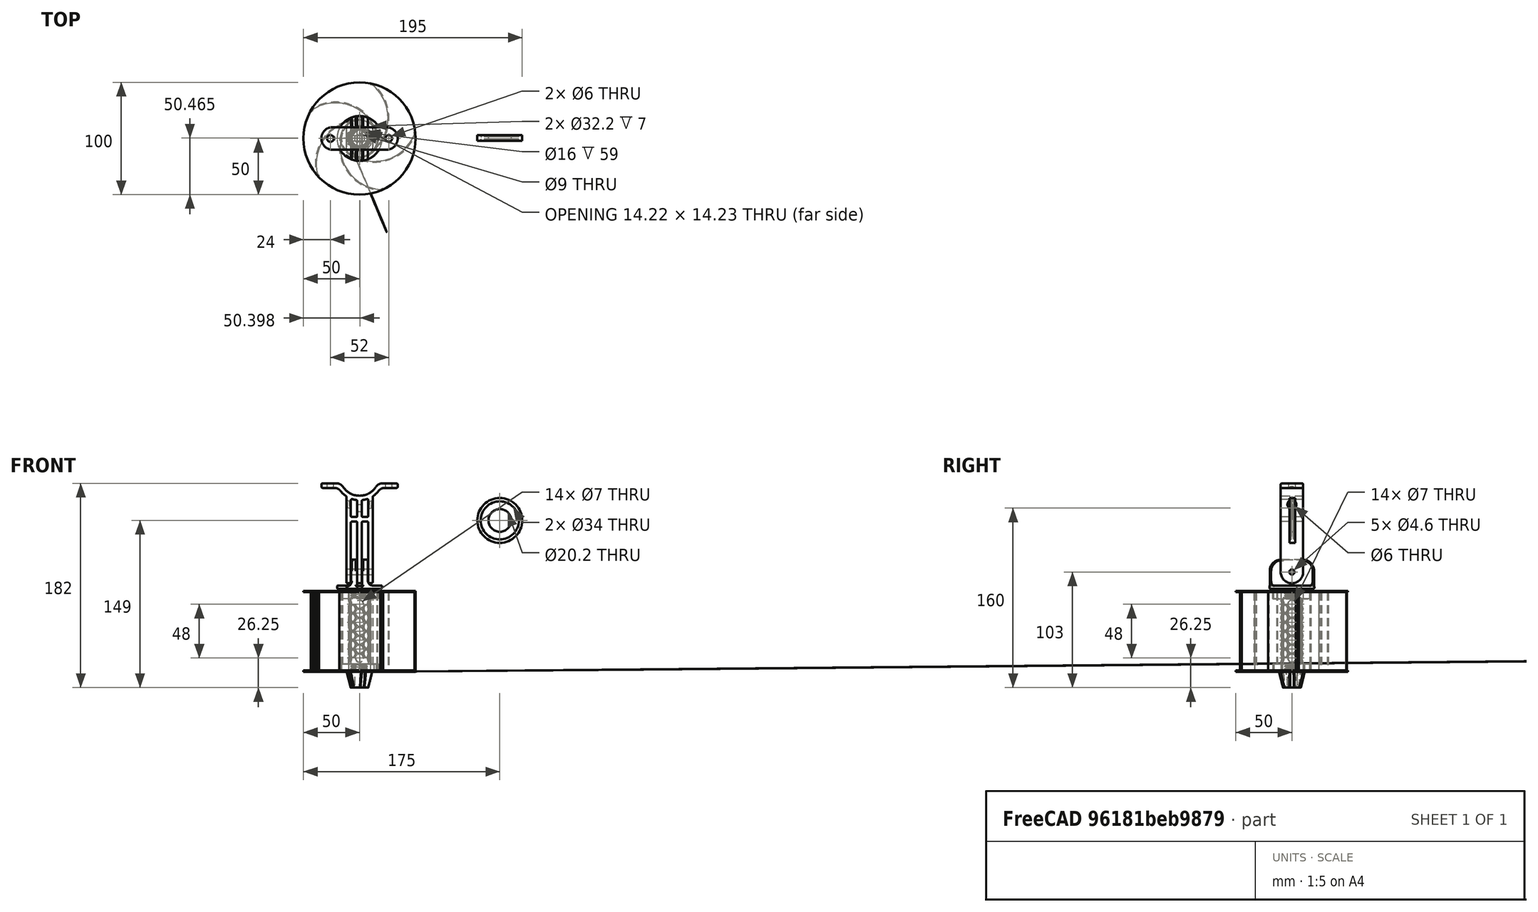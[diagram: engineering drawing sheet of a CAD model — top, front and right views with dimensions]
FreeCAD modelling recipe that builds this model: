
FCSTD DOCUMENT  (FreeCAD 1.1R40077 (Git))
Label: NES-sampler
License: All rights reserved
LicenseURL: http://en.wikipedia.org/wiki/All_rights_reserved
objects: Part::Cylinder×77, Part::MultiFuse×25, Part::Cut×25, Part::Box×21, Part::Fillet×11, Part::Part2DObjectPython×6, Part::Cone×6, Part::MultiCommon×5, Part::Helix×4, Part::Sweep×4
note: 184 computed .brp shape members not serialized (recipe doc carries the construction recipe); baked Part::Feature solids carry a one-line shape summary decoded from their .brp

FEATURE [Part::Cylinder] Cylinder079
  Angle = 360
  AttacherType = Attacher::AttachEngine3D
  FirstAngle = 0
  Height = 26
  Placement = pos=(0,13,62) rot=(1,0,0;1.5708rad)
  Radius = 3.5
  SecondAngle = 0
FEATURE [Part::Cylinder] Cylinder082
  Angle = 360
  AttacherType = Attacher::AttachEngine3D
  FirstAngle = 0
  Height = 26
  Placement = pos=(0,13,22) rot=(1,0,0;1.5708rad)
  Radius = 3.5
  SecondAngle = 0
FEATURE [Part::Cylinder] Cylinder083
  Angle = 360
  AttacherType = Attacher::AttachEngine3D
  FirstAngle = 0
  Height = 26
  Placement = pos=(0,13,54) rot=(1,0,0;1.5708rad)
  Radius = 3.5
  SecondAngle = 0
FEATURE [Part::Cylinder] Cylinder084
  Angle = 360
  AttacherType = Attacher::AttachEngine3D
  FirstAngle = 0
  Height = 26
  Placement = pos=(0,13,46) rot=(1,0,0;1.5708rad)
  Radius = 3.5
  SecondAngle = 0
FEATURE [Part::Cylinder] Cylinder085
  Angle = 360
  AttacherType = Attacher::AttachEngine3D
  FirstAngle = 0
  Height = 26
  Placement = pos=(0,13,30) rot=(1,0,0;1.5708rad)
  Radius = 3.5
  SecondAngle = 0
FEATURE [Part::Cylinder] Cylinder086
  Angle = 360
  AttacherType = Attacher::AttachEngine3D
  FirstAngle = 0
  Height = 26
  Placement = pos=(0,13,62) rot=(1,0,0;1.5708rad)
  Radius = 3.5
  SecondAngle = 0
FEATURE [Part::Cylinder] Cylinder087
  Angle = 360
  AttacherType = Attacher::AttachEngine3D
  FirstAngle = 0
  Height = 26
  Placement = pos=(0,13,14) rot=(1,0,0;1.5708rad)
  Radius = 3.5
  SecondAngle = 0
FEATURE [Part::Cylinder] Cylinder088
  Angle = 360
  AttacherType = Attacher::AttachEngine3D
  FirstAngle = 0
  Height = 26
  Placement = pos=(0,13,38) rot=(1,0,0;1.5708rad)
  Radius = 3.5
  SecondAngle = 0
FEATURE [Part::Cylinder] Cylinder104
  Angle = 360
  AttacherType = Attacher::AttachEngine3D
  FirstAngle = 0
  Height = 77
  Placement = pos=(0,0,3) rot=(0,0,1;0rad)
  Radius = 8
  SecondAngle = 0
FEATURE [Part::Cylinder] Cylinder106
  Angle = 360
  AttacherType = Attacher::AttachEngine3D
  FirstAngle = 0
  Height = 73
  Placement = pos=(0,0,4.26) rot=(0,0,1;0rad)
  Radius = 9.8
  SecondAngle = 0
FEATURE [Part::Cylinder] Cylinder166
  Angle = 360
  AttacherType = Attacher::AttachEngine3D
  FirstAngle = 0
  Height = 26
  Placement = pos=(0,13,53) rot=(1,0,0;1.5708rad)
  Radius = 3.5
  SecondAngle = 0
FEATURE [Part::Cylinder] Cylinder167
  Angle = 360
  AttacherType = Attacher::AttachEngine3D
  FirstAngle = 0
  Height = 26
  Placement = pos=(0,13,21) rot=(1,0,0;1.5708rad)
  Radius = 3.5
  SecondAngle = 0
FEATURE [Part::Cylinder] Cylinder168
  Angle = 360
  AttacherType = Attacher::AttachEngine3D
  FirstAngle = 0
  Height = 26
  Placement = pos=(0,13,29) rot=(1,0,0;1.5708rad)
  Radius = 3.5
  SecondAngle = 0
FEATURE [Part::Cylinder] Cylinder169
  Angle = 360
  AttacherType = Attacher::AttachEngine3D
  FirstAngle = 0
  Height = 26
  Placement = pos=(0,13,37) rot=(1,0,0;1.5708rad)
  Radius = 3.5
  SecondAngle = 0
FEATURE [Part::Cylinder] Cylinder170
  Angle = 360
  AttacherType = Attacher::AttachEngine3D
  FirstAngle = 0
  Height = 26
  Placement = pos=(0,13,61) rot=(1,0,0;1.5708rad)
  Radius = 3.5
  SecondAngle = 0
FEATURE [Part::Cylinder] Cylinder171
  Angle = 360
  AttacherType = Attacher::AttachEngine3D
  FirstAngle = 0
  Height = 26
  Placement = pos=(0,13,45) rot=(1,0,0;1.5708rad)
  Radius = 3.5
  SecondAngle = 0
FEATURE [Part::Cylinder] Cylinder172
  Angle = 360
  AttacherType = Attacher::AttachEngine3D
  FirstAngle = 0
  Height = 26
  Placement = pos=(0,13,22) rot=(1,0,0;1.5708rad)
  Radius = 3.5
  SecondAngle = 0
FEATURE [Part::Cylinder] Cylinder173
  Angle = 360
  AttacherType = Attacher::AttachEngine3D
  FirstAngle = 0
  Height = 26
  Placement = pos=(0,13,30) rot=(1,0,0;1.5708rad)
  Radius = 3.5
  SecondAngle = 0
FEATURE [Part::Cylinder] Cylinder174
  Angle = 360
  AttacherType = Attacher::AttachEngine3D
  FirstAngle = 0
  Height = 26
  Placement = pos=(0,13,38) rot=(1,0,0;1.5708rad)
  Radius = 3.5
  SecondAngle = 0
FEATURE [Part::Cylinder] Cylinder175
  Angle = 360
  AttacherType = Attacher::AttachEngine3D
  FirstAngle = 0
  Height = 26
  Placement = pos=(0,13,46) rot=(1,0,0;1.5708rad)
  Radius = 3.5
  SecondAngle = 0
FEATURE [Part::Cylinder] Cylinder176
  Angle = 360
  AttacherType = Attacher::AttachEngine3D
  FirstAngle = 0
  Height = 26
  Placement = pos=(0,13,54) rot=(1,0,0;1.5708rad)
  Radius = 3.5
  SecondAngle = 0
FEATURE [Part::Cylinder] Cylinder177
  Angle = 360
  AttacherType = Attacher::AttachEngine3D
  FirstAngle = 0
  Height = 26
  Placement = pos=(0,13,14) rot=(1,0,0;1.5708rad)
  Radius = 3.5
  SecondAngle = 0
FEATURE [Part::Cylinder] Cylinder178
  Angle = 360
  AttacherType = Attacher::AttachEngine3D
  FirstAngle = 0
  Height = 26
  Placement = pos=(0,13,62) rot=(1,0,0;1.5708rad)
  Radius = 3.5
  SecondAngle = 0
FEATURE [Part::Cylinder] Cylinder179
  Angle = 360
  AttacherType = Attacher::AttachEngine3D
  FirstAngle = 0
  Height = 26
  Placement = pos=(0,13,29) rot=(1,0,0;1.5708rad)
  Radius = 3.5
  SecondAngle = 0
FEATURE [Part::Cylinder] Cylinder180
  Angle = 360
  AttacherType = Attacher::AttachEngine3D
  FirstAngle = 0
  Height = 26
  Placement = pos=(0,13,45) rot=(1,0,0;1.5708rad)
  Radius = 3.5
  SecondAngle = 0
FEATURE [Part::Cylinder] Cylinder181
  Angle = 360
  AttacherType = Attacher::AttachEngine3D
  FirstAngle = 0
  Height = 26
  Placement = pos=(0,13,61) rot=(1,0,0;1.5708rad)
  Radius = 3.5
  SecondAngle = 0
FEATURE [Part::Cylinder] Cylinder182
  Angle = 360
  AttacherType = Attacher::AttachEngine3D
  FirstAngle = 0
  Height = 26
  Placement = pos=(0,13,37) rot=(1,0,0;1.5708rad)
  Radius = 3.5
  SecondAngle = 0
FEATURE [Part::Cylinder] Cylinder183
  Angle = 360
  AttacherType = Attacher::AttachEngine3D
  FirstAngle = 0
  Height = 26
  Placement = pos=(0,13,21) rot=(1,0,0;1.5708rad)
  Radius = 3.5
  SecondAngle = 0
FEATURE [Part::Cylinder] Cylinder184
  Angle = 360
  AttacherType = Attacher::AttachEngine3D
  FirstAngle = 0
  Height = 26
  Placement = pos=(0,13,53) rot=(1,0,0;1.5708rad)
  Radius = 3.5
  SecondAngle = 0
FEATURE [Part::MultiFuse] Fusion113
  Placement = pos=(0,0,2) rot=(0,0,1;0rad)
  Shapes = -> [Cylinder088,Cylinder079,Cylinder083,Cylinder082,Cylinder085,Cylinder087,Cylinder086,Cylinder084]
FEATURE [Part::MultiFuse] Fusion114
  Placement = pos=(0,0,-1) rot=(0,0,1;0.785398rad)
  Shapes = -> [Cylinder169,Cylinder168,Cylinder171,Cylinder170,Cylinder167,Cylinder166]
FEATURE [Part::MultiFuse] Fusion115
  Placement = pos=(0,0,-1) rot=(0,0,-1;0.785398rad)
  Shapes = -> [Cylinder182,Cylinder179,Cylinder180,Cylinder181,Cylinder183,Cylinder184]
FEATURE [Part::MultiFuse] Fusion116
  Placement = pos=(0,0,2) rot=(0,0,1;1.5708rad)
  Shapes = -> [Cylinder177,Cylinder172,Cylinder173,Cylinder174,Cylinder175,Cylinder176,Cylinder178]
FEATURE [Part::MultiFuse] Fusion190
  Placement = pos=(0,0,0.5) rot=(0,0,1;0rad)
  Shapes = -> [Fusion116,Fusion115,Fusion114,Fusion113]
FEATURE [Part::MultiFuse] Fusion191
  Shapes = -> [Cylinder104,Fusion190]
FEATURE [Part::Cut] Cut036
  Base = -> Cylinder106
  Placement = pos=(0,0,35.75) rot=(0,0,1;0rad)
  Tool = -> Fusion191
FEATURE [Part::Helix] Helix001
  Angle = 0
  AttacherType = Attacher::AttachEngine3D
  Height = 10
  Length = 231.123
  LocalCoord = 0
  Pitch = 2
  Radius = 7.35
  SegmentLength = 1
  Style = 0
  expr: AttachmentOffset = VThreadProfile001.AttachmentOffset
  expr: Height = VThreadProfile001.ThreadCount * VThreadProfile001.Pitch
  expr: MapMode = VThreadProfile001.MapMode
  expr: MapPathParameter = VThreadProfile001.MapPathParameter
  expr: MapReversed = VThreadProfile001.MapReversed
  expr: Pitch = VThreadProfile001.Pitch
  expr: SegmentLength = 1
FEATURE [Part::Part2DObjectPython] VThreadProfile001  # Draft 2D object (typed FeaturePython)
  Area = 186.808
  Closed = true
  Continuity = C2
  Height = 10
  Helix = Helix
  Instructions = Expand this with the ... button to view instructions | Sweep this object along a helix of the same pitch to produce your thread. | It is recommended to make the helix in the ThreadProfile workbench. | If there is an active Body the ThreadProfile object will be put into it.,If not it can be dragged and dropped into the body later. | If there is an active Body when the helix is made there will be made a ShapeBinder for it | For internal threads you will need to cut the Sweep object out of a cylinder, or if using Part Design sweep it as a Subtractive Pipe. | Always use Frenet mode | I have provided some presets, but it is possible there could be some errors.  Double check for mission critical applications. | Also, the tolerances might be different from what you wish to have.  I believe the internal minor diameters are all minimum and the external are all maximum.
  InternalOrExternal = 1
  MakeFace = true
  MinorDiameter = 14.5
  Parameterization = 1
  Pitch = 2
  Points = (66) [(7.21184,0.695393,0),(7.07086,1.3764,0),(6.87744,2.04019,0),(6.62901,2.68241,0),(6.32585,3.2984,0),(5.96952,3.88346,0),(5.56241,4.43304,0),+59 more]
  Presets = 0
  Quality = 11
  ThreadCount = 5
  Variants = 0
  Version = 1.89
  external2S_data = [-0.00461051,-0.00886426,-0.0128148,-0.0165028,-0.0199596,-0.0232105,-0.0262759,-0.0291725,-0.0319145,-0.0345137,-0.0369805,-0.0393235,-0.0415505,-0.0436681,-0.0456823,-0.0475981,-0.0494204,-0.0511532,-0.0528003,-0.0543649,-0.0558502,+698 more]
  external3S_data = [-0.00677828,-0.0128149,-0.0182584,-0.0232106,-0.0277444,-0.0319145,-0.0357632,-0.0393236,-0.0426227,-0.0456823,-0.0485208,-0.0511533,-0.0535928,-0.0558503,-0.0579353,-0.059856,-0.0616195,-0.0632319,-0.0646984,-0.0660239,-0.0672123,+698 more]
  external45_data = [-0.00137363,-0.00271738,-0.00403219,-0.00531893,-0.00657844,-0.00781148,-0.00901878,-0.010201,-0.0113589,-0.012493,-0.0136039,-0.0146921,-0.0157583,-0.0168028,-0.0178261,-0.0188288,-0.0198112,-0.0207738,-0.0217169,-0.0226409,-0.0235462,+698 more]
  external_data = [-0.00235387,-0.00461052,-0.00677828,-0.00886428,-0.0108747,-0.0128149,-0.0146895,-0.0165028,-0.0182584,-0.0199597,-0.0216095,-0.0232106,-0.0247653,-0.0262759,-0.0277444,-0.0291725,-0.0305621,-0.0319145,-0.0332313,-0.0345138,-0.0357632,+698 more]
  internal2S_data = [0,0,0,0,0,0,0,0,0,0,0,0,0,0,0,0,0,0,0,0,0,0,0,0,0,0,0,0,0,0,0,0,0,0,0,0,0,0,0,0,0,0,0,0,0,0,0,0,0,0,0,0,0,0,0,0,0,0,0,0,0,0,0,0,0,0,0,0,0,0,0,0,0,0,0,0,0,0,0,0,0,0,0,0,0,0,0,0,0,0,0.00481128,0.00962256,0.0144338,0.0192451,0.0240564,+624 more]
  internal3S_data = [0,0,0,0,0,0,0,0,0,0,0,0,0,0,0,0,0,0,0,0,0,0,0,0,0,0,0,0,0,0,0,0,0,0,0,0,0,0,0,0,0,0,0,0,0,0,0,0,0,0,0,0,0,0,0,0,0,0,0,0,0.00721688,0.0144338,0.0216506,0.0288675,0.0360844,0.0433013,0.0505181,0.057735,0.0649519,0.0721688,0.0793857,0.0866025,+647 more]
  internal45_data = [0,0,0,0,0,0,0,0,0,0,0,0,0,0,0,0,0,0,0,0,0,0,0,0,0,0,0,0,0,0,0,0,0,0,0,0,0,0,0,0,0,0,0,0,0,0,0,0,0,0,0,0,0,0,0,0,0,0,0,0,0,0,0,0,0,0,0,0,0,0,0,0,0,0,0,0,0,0,0,0,0,0,0,0,0,0,0,0,0,0,0,0,0,0,0,0,0,0,0,0,0,0,0,0,0,0,0,0,0,0,0,0,0,0,0,0,0,0,0,0,+599 more]
  internal_data = [0,0,0,0,0,0,0,0,0,0,0,0,0,0,0,0,0,0,0,0,0,0,0,0,0,0,0,0,0,0,0,0,0,0,0,0,0,0,0,0,0,0,0,0,0,0,0,0,0,0,0,0,0,0,0,0,0,0,0,0,0,0,0,0,0,0,0,0,0,0,0,0,0,0,0,0,0,0,0,0,0,0,0,0,0,0,0,0,0,0,0,0,0,0,0,0,0,0,0,0,0,0,0,0,0,0,0,0,0,0,0,0,0,0,0,0,0,0,0,0,+599 more]
  preset_names = <blob: 3959 chars omitted>
  presets_data = [0,0,0,2.20878,24.1173,24.6888,0.25,0.693,0.729,0.25,0.793,0.829,0.25,0.893,0.929,0.3,1.032,1.075,0.35,1.171,1.221,0.35,1.371,1.421,0.4,1.509,1.567,0.45,1.648,1.713,0.45,1.948,2.013,0.5,2.387,2.459,0.6,2.764,2.85,0.7,3.141,3.242,0.75,3.58,+712 more]
FEATURE [Part::Sweep] Sweep001  label="m16 wide"
  Frenet = true
  Placement = pos=(0,0,37) rot=(0,0,1;0rad)
  Sections = -> [VThreadProfile001]
  Solid = true
  Spine = -> Helix001 [Edge1,Edge2,Edge3,Edge4,Edge5]
  Transition = 1
FEATURE [Part::Cylinder] Cylinder
  Angle = 360
  AttacherType = Attacher::AttachEngine3D
  FirstAngle = 0
  Height = 7
  Placement = pos=(0,0,40) rot=(0,0,1;0rad)
  Radius = 9
  SecondAngle = 0
FEATURE [Part::Helix] Helix002
  Angle = 0
  AttacherType = Attacher::AttachEngine3D
  Height = 10
  Length = 231.123
  LocalCoord = 0
  Pitch = 2
  Radius = 7.35
  SegmentLength = 1
  Style = 0
  expr: AttachmentOffset = VThreadProfile002.AttachmentOffset
  expr: Height = VThreadProfile002.ThreadCount * VThreadProfile002.Pitch
  expr: MapMode = VThreadProfile002.MapMode
  expr: MapPathParameter = VThreadProfile002.MapPathParameter
  expr: MapReversed = VThreadProfile002.MapReversed
  expr: Pitch = VThreadProfile002.Pitch
  expr: SegmentLength = 1
FEATURE [Part::Part2DObjectPython] VThreadProfile002  # Draft 2D object (typed FeaturePython)
  Area = 186.808
  Closed = true
  Continuity = C2
  Height = 10
  Helix = Helix
  Instructions = <same value as first occurrence — deduplicated (x6 in doc)>
  InternalOrExternal = 1
  MakeFace = true
  MinorDiameter = 14.5
  Parameterization = 1
  Pitch = 2
  Points = (66) [(7.21184,0.695393,0),(7.07086,1.3764,0),(6.87744,2.04019,0),(6.62901,2.68241,0),(6.32585,3.2984,0),(5.96952,3.88346,0),(5.56241,4.43304,0),+59 more]
  Presets = 0
  Quality = 11
  ThreadCount = 5
  Variants = 0
  Version = 1.89
  external2S_data = <same value as first occurrence — deduplicated (x6 in doc)>
  external3S_data = <same value as first occurrence — deduplicated (x6 in doc)>
  external45_data = <same value as first occurrence — deduplicated (x6 in doc)>
  external_data = <same value as first occurrence — deduplicated (x6 in doc)>
  internal2S_data = <same value as first occurrence — deduplicated (x6 in doc)>
  internal3S_data = <same value as first occurrence — deduplicated (x6 in doc)>
  internal45_data = <same value as first occurrence — deduplicated (x6 in doc)>
  internal_data = <same value as first occurrence — deduplicated (x6 in doc)>
  preset_names = <blob: 3959 chars omitted>
  presets_data = <same value as first occurrence — deduplicated (x6 in doc)>
FEATURE [Part::Sweep] Sweep002  label="m16 wide001"
  Frenet = true
  Placement = pos=(0,0,106) rot=(0,0,1;0rad)
  Sections = -> [VThreadProfile002]
  Solid = true
  Spine = -> Helix002 [Edge1,Edge2,Edge3,Edge4,Edge5]
  Transition = 1
FEATURE [Part::Cylinder] Cylinder272
  Angle = 360
  AttacherType = Attacher::AttachEngine3D
  FirstAngle = 0
  Height = 7
  Placement = pos=(0,0,106) rot=(0,0,1;0rad)
  Radius = 9
  SecondAngle = 0
FEATURE [Part::MultiFuse] Fusion196
  Shapes = -> [Cut036,Cylinder,Cylinder272]
FEATURE [Part::MultiFuse] Fusion197
  Shapes = -> [Sweep001,Sweep002]
FEATURE [Part::Cut] Cut119
  Base = -> Fusion196
  Tool = -> Fusion197
FEATURE [Part::Fillet] Fillet002  label="core"
  Base = -> Cut119
  EdgeLinks = -> Cut119 [Edge9,Edge11,Edge13,Edge15,Edge17,Edge19,Edge21,Edge24,Edge25,Edge26,Edge28,Edge30,Edge32,Edge34,Edge36,Edge38,Edge39,Edge40,Edge41,Edge42,Edge43,Edge44,Edge45,Edge46,Edge47,Edge48,Edge49,Edge50,Edge51,Edge52,Edge53,Edge54,Edge55,Edge56,Edge57,Edge58,Edge59,Edge60,Edge61,Edge62,+80 more]
  Edges = 120 edges r=0.2: [Edge9,Edge11,Edge13,Edge15,Edge17,Edge19,Edge21,Edge24,Edge25,Edge26,Edge28,Edge30,Edge32,Edge34,Edge36,Edge38,Edge39,Edge40,Edge41,Edge42,Edge43,Edge44,Edge45,Edge46,Edge47,Edge48,Edge49,Edge50,Edge51,Edge52,Edge53,Edge54,Edge55,Edge56,Edge57,Edge58,Edge59,Edge60,Edge61,Edge62,Edge63,Edge64,Edge65,+77 more]
FEATURE [Part::Cylinder] Cylinder435
  Angle = 360
  AttacherType = Attacher::AttachEngine3D
  FirstAngle = 0
  Height = 2
  Radius = 20
  SecondAngle = 0
FEATURE [Part::Cylinder] Cylinder436
  Angle = 360
  AttacherType = Attacher::AttachEngine3D
  FirstAngle = 0
  Height = 3
  Radius = 10.1
  SecondAngle = 0
FEATURE [Part::Cut] Cut219  label="guiding aid000"
  Base = -> Cylinder435
  Placement = pos=(125,1.5,175) rot=(1,0,0;1.5708rad)
  Tool = -> Cylinder436
FEATURE [Part::Box] Box057  label="Cube057"
  AttacherType = Attacher::AttachEngine3D
  Height = 24
  Length = 4.4
  Placement = pos=(-2.2,-21,114.5) rot=(0,0,1;0rad)
  Width = 42
FEATURE [Part::Box] Box058  label="Cube058"
  AttacherType = Attacher::AttachEngine3D
  Height = 19
  Length = 7
  Placement = pos=(7.5,-19,119) rot=(0,0,1;0rad)
  Width = 38
FEATURE [Part::Box] Box059  label="Cube059"
  AttacherType = Attacher::AttachEngine3D
  Height = 19
  Length = 7
  Placement = pos=(-14.5,-19,119) rot=(0,0,1;0rad)
  Width = 38
FEATURE [Part::Box] Box060  label="Cube060"
  AttacherType = Attacher::AttachEngine3D
  Height = 23
  Length = 9
  Placement = pos=(-20.5,-19,115) rot=(0,0,1;0rad)
  Width = 38
FEATURE [Part::Box] Box061  label="Cube061"
  AttacherType = Attacher::AttachEngine3D
  Height = 23
  Length = 9
  Placement = pos=(11.5,-19,115) rot=(0,0,1;0rad)
  Width = 38
FEATURE [Part::Cylinder] Cylinder437
  Angle = 360
  AttacherType = Attacher::AttachEngine3D
  FirstAngle = 0
  Height = 26
  Placement = pos=(0,0,113.5) rot=(0,0,1;0rad)
  Radius = 20
  SecondAngle = 0
FEATURE [Part::Cylinder] Cylinder438
  Angle = 360
  AttacherType = Attacher::AttachEngine3D
  FirstAngle = 0
  Height = 24
  Placement = pos=(-12,0,127) rot=(0,1,0;1.5708rad)
  Radius = 2.3
  SecondAngle = 0
FEATURE [Part::Cylinder] Cylinder439
  Angle = 360
  AttacherType = Attacher::AttachEngine3D
  FirstAngle = 0
  Height = 38
  Placement = pos=(11.5,19,119) rot=(1,0,0;1.5708rad)
  Radius = 4
  SecondAngle = 0
FEATURE [Part::Cylinder] Cylinder440
  Angle = 360
  AttacherType = Attacher::AttachEngine3D
  FirstAngle = 0
  Height = 38
  Placement = pos=(-11.5,19,119) rot=(1,0,0;1.5708rad)
  Radius = 4
  SecondAngle = 0
FEATURE [Part::Cylinder] Cylinder442
  Angle = 360
  AttacherType = Attacher::AttachEngine3D
  FirstAngle = 0
  Height = 1
  Placement = pos=(0,0,112) rot=(0,0,1;0rad)
  Radius = 10
  SecondAngle = 0
FEATURE [Part::MultiFuse] Fusion237
  Placement = pos=(0,0,1.5) rot=(0,0,1;0rad)
  Shapes = -> [Cylinder438,Cylinder439,Cylinder440,Box057,Box058,Box059,Box060,Box061]
FEATURE [Part::Helix] Helix004
  Angle = 0
  AttacherType = Attacher::AttachEngine3D
  Height = 10
  Length = 231.123
  LocalCoord = 0
  Pitch = 2
  Radius = 7.35
  SegmentLength = 1
  Style = 0
  expr: AttachmentOffset = VThreadProfile005.AttachmentOffset
  expr: Height = VThreadProfile006.ThreadCount * VThreadProfile006.Pitch
  expr: MapMode = VThreadProfile005.MapMode
  expr: MapPathParameter = VThreadProfile005.MapPathParameter
  expr: MapReversed = VThreadProfile005.MapReversed
  expr: Pitch = VThreadProfile006.Pitch
  expr: SegmentLength = 1
FEATURE [Part::Part2DObjectPython] VThreadProfile005  # Draft 2D object (typed FeaturePython)
  Area = 163.406
  Closed = true
  Continuity = C2
  Height = 6.5
  Helix = Helix
  Instructions = <same value as first occurrence — deduplicated (x6 in doc)>
  InternalOrExternal = 1
  MakeFace = true
  MinorDiameter = 13.5
  Parameterization = 1
  Pitch = 2
  Points = (66) [(6.71415,0.647404,0),(6.58007,1.28086,0),(6.39808,1.89799,0),(6.16552,2.49486,0),(5.8825,3.06723,0),(5.55041,3.6108,0),(5.1714,4.12141,0),+59 more]
  Presets = 0
  Quality = 11
  ThreadCount = 3.25
  Variants = 0
  Version = 1.89
  external2S_data = <same value as first occurrence — deduplicated (x6 in doc)>
  external3S_data = <same value as first occurrence — deduplicated (x6 in doc)>
  external45_data = <same value as first occurrence — deduplicated (x6 in doc)>
  external_data = <same value as first occurrence — deduplicated (x6 in doc)>
  internal2S_data = <same value as first occurrence — deduplicated (x6 in doc)>
  internal3S_data = <same value as first occurrence — deduplicated (x6 in doc)>
  internal45_data = <same value as first occurrence — deduplicated (x6 in doc)>
  internal_data = <same value as first occurrence — deduplicated (x6 in doc)>
  preset_names = <blob: 3959 chars omitted>
  presets_data = <same value as first occurrence — deduplicated (x6 in doc)>
FEATURE [Part::Sweep] Sweep004  label="m16 thread002"
  Frenet = true
  Placement = pos=(0,0,105) rot=(0,0,1;0rad)
  Sections = -> [VThreadProfile005]
  Solid = true
  Spine = -> Helix004 [Edge1,Edge2,Edge3,Edge4]
  Transition = 1
FEATURE [Part::MultiFuse] Fusion238  label="top-screw-thread"
  Placement = pos=(0,0,1) rot=(0,0,1;0rad)
  Shapes = -> [Cylinder442,Sweep004]
FEATURE [Part::Cut] Cut220
  Base = -> Cylinder437
  Tool = -> Fusion237
FEATURE [Part::Fillet] Fillet012
  Base = -> Cut220
  EdgeLinks = -> Cut220 [Edge6,Edge10,Edge16,Edge20]
  Edges = 4 edges r=10: [Edge6,Edge10,Edge16,Edge20]
FEATURE [Part::Fillet] Fillet013
  Base = -> Fillet012
  EdgeLinks = -> Fillet012 [Edge32,Edge36]
  Edges = 2 edges r=1: [Edge32,Edge36]
FEATURE [Part::Fillet] Fillet014  label="top-screw-head"
  Base = -> Fillet013
  EdgeLinks = -> Fillet013 [Edge11,Edge13,Edge19,Edge23]
  Edges = 4 edges r=1: [Edge11,Edge13,Edge19,Edge23]
  Placement = pos=(0,0,0.5) rot=(0,0,1;0rad)
FEATURE [Part::Box] Box075  label="Cube075"
  AttacherType = Attacher::AttachEngine3D
  Height = 75
  Length = 4
  Placement = pos=(-2,-10,73) rot=(0,0,1;0rad)
  Width = 20
FEATURE [Part::Box] Box076  label="Cube076"
  AttacherType = Attacher::AttachEngine3D
  Height = 4
  Length = 68
  Placement = pos=(-34,-10,158) rot=(0,0,1;0rad)
  Width = 20
FEATURE [Part::Box] Box077  label="Cube077"
  AttacherType = Attacher::AttachEngine3D
  Height = 30
  Length = 60
  Placement = pos=(-30,-10,162) rot=(0,0,1;0rad)
  Width = 20
FEATURE [Part::Cylinder] Cylinder471
  Angle = 360
  AttacherType = Attacher::AttachEngine3D
  FirstAngle = 0
  Height = 24
  Placement = pos=(-12,0,83) rot=(0,1,0;1.5708rad)
  Radius = 2.3
  SecondAngle = 0
FEATURE [Part::Cylinder] Cylinder472
  Angle = 360
  AttacherType = Attacher::AttachEngine3D
  FirstAngle = 0
  Height = 20
  Placement = pos=(0,10,168.5) rot=(1,0,0;1.5708rad)
  Radius = 21.5
  SecondAngle = 0
FEATURE [Part::Cylinder] Cylinder473
  Angle = 360
  AttacherType = Attacher::AttachEngine3D
  FirstAngle = 0
  Height = 20
  Placement = pos=(0,10,168.5) rot=(1,0,0;1.5708rad)
  Radius = 17.5
  SecondAngle = 0
FEATURE [Part::Cylinder] Cylinder474
  Angle = 360
  AttacherType = Attacher::AttachEngine3D
  FirstAngle = 0
  Height = 6
  Placement = pos=(26,0,157) rot=(0,0,1;0rad)
  Radius = 3
  SecondAngle = 0
FEATURE [Part::Cylinder] Cylinder475
  Angle = 360
  AttacherType = Attacher::AttachEngine3D
  FirstAngle = 0
  Height = 6
  Placement = pos=(-26,0,157) rot=(0,0,1;0rad)
  Radius = 3
  SecondAngle = 0
FEATURE [Part::Cylinder] Cylinder476
  Angle = 360
  AttacherType = Attacher::AttachEngine3D
  FirstAngle = 0
  Height = 6
  Placement = pos=(-3,0,140) rot=(0,1,0;1.5708rad)
  Radius = 3
  SecondAngle = 0
FEATURE [Part::Box] Box078  label="Cube078"
  AttacherType = Attacher::AttachEngine3D
  Height = 79
  Length = 4
  Placement = pos=(7.75,-10,73) rot=(0,0,1;0rad)
  Width = 20
FEATURE [Part::Box] Box079  label="Cube079"
  AttacherType = Attacher::AttachEngine3D
  Height = 79
  Length = 4
  Placement = pos=(-11.75,-10,73) rot=(0,0,1;0rad)
  Width = 20
FEATURE [Part::Cylinder] Cylinder477
  Angle = 360
  AttacherType = Attacher::AttachEngine3D
  FirstAngle = 0
  Height = 7
  Placement = pos=(6.5,0,142) rot=(0,1,0;1.309rad)
  Radius = 3
  SecondAngle = 0
FEATURE [Part::Cylinder] Cylinder478
  Angle = 360
  AttacherType = Attacher::AttachEngine3D
  FirstAngle = 0
  Height = 7
  Placement = pos=(-12.75,0,144) rot=(0,1,0;1.8326rad)
  Radius = 3
  SecondAngle = 0
FEATURE [Part::Box] Box080  label="Cube080"
  AttacherType = Attacher::AttachEngine3D
  Height = 4
  Length = 22
  Placement = pos=(-11,-10,128) rot=(0,0,1;0rad)
  Width = 20
FEATURE [Part::MultiFuse] Fusion250
  Shapes = -> [Box075,Box076,Cylinder472,Box078,Box079,Box080]
FEATURE [Part::MultiFuse] Fusion251
  Shapes = -> [Box077,Cylinder471,Cylinder473,Cylinder474,Cylinder475,Cylinder476,Cylinder477,Cylinder478]
FEATURE [Part::Cut] Cut226
  Base = -> Fusion250
  Tool = -> Fusion251
FEATURE [Part::Fillet] Fillet030
  Base = -> Cut226
  EdgeLinks = -> Cut226 [Edge8,Edge9,Edge47,Edge49,Edge100,Edge101,Edge158,Edge161,Edge169,Edge173]
  Edges = 10 edges r=9.9: [Edge8,Edge9,Edge47,Edge49,Edge100,Edge101,Edge158,Edge161,Edge169,Edge173]
FEATURE [Part::Fillet] Fillet031
  Base = -> Fillet030
  EdgeLinks = -> Fillet030 [Edge142,Edge159,Edge161,Edge164]
  Edges = 4 edges r=7: [Edge142,Edge159,Edge161,Edge164]
FEATURE [Part::Fillet] Fillet032
  Base = -> Fillet031
  EdgeLinks = -> Fillet031 [Edge20,Edge40,Edge41,Edge50,Edge53,Edge54,Edge62,Edge81,Edge89,Edge105,Edge109,Edge117,Edge125,Edge133,Edge141,Edge144,Edge159,Edge169,Edge193,Edge195,Edge200,Edge212,Edge217,Edge224]
  Edges = 24 edges r=1: [Edge20,Edge40,Edge41,Edge50,Edge53,Edge54,Edge62,Edge81,Edge89,Edge105,Edge109,Edge117,Edge125,Edge133,Edge141,Edge144,Edge159,Edge169,Edge193,Edge195,Edge200,Edge212,Edge217,Edge224]
FEATURE [Part::Fillet] Fillet033  label="fortified-branch-mounter-zip-tie"
  Base = -> Fillet032
  EdgeLinks = -> Fillet032 [Edge7,Edge28,Edge67,Edge75,Edge79,Edge85,Edge119,Edge139,Edge140,Edge187,Edge199,Edge200,Edge213,Edge218,Edge253]
  Edges = 15 edges r=1: [Edge7,Edge28,Edge67,Edge75,Edge79,Edge85,Edge119,Edge139,Edge140,Edge187,Edge199,Edge200,Edge213,Edge218,Edge253]
  Placement = pos=(0,0,46) rot=(0,0,1;0rad)
FEATURE [Part::Box] Box081  label="Cube081"
  AttacherType = Attacher::AttachEngine3D
  Height = 70
  Length = 61
  Placement = pos=(0,-102,41) rot=(0,0,1;0rad)
  Width = 122
FEATURE [Part::Box] Box082  label="Cube082"
  AttacherType = Attacher::AttachEngine3D
  Height = 70
  Length = 61
  Placement = pos=(0,-102,41) rot=(0,0,1;0rad)
  Width = 122
FEATURE [Part::Box] Box083  label="Cube083"
  AttacherType = Attacher::AttachEngine3D
  Height = 70
  Length = 61
  Placement = pos=(0,-102,41) rot=(0,0,1;0rad)
  Width = 122
FEATURE [Part::Box] Box084  label="Cube084"
  AttacherType = Attacher::AttachEngine3D
  Height = 70
  Length = 61
  Placement = pos=(0,-102,41) rot=(0,0,1;0rad)
  Width = 122
FEATURE [Part::Box] Box085  label="Cube085"
  AttacherType = Attacher::AttachEngine3D
  Height = 70
  Length = 61
  Placement = pos=(0,-102,41) rot=(0,0,1;0rad)
  Width = 122
FEATURE [Part::Cylinder] Cylinder479
  Angle = 360
  AttacherType = Attacher::AttachEngine3D
  FirstAngle = 0
  Height = 7
  Radius = 16.1
  SecondAngle = 0
FEATURE [Part::Cylinder] Cylinder480
  Angle = 360
  AttacherType = Attacher::AttachEngine3D
  FirstAngle = 0
  Height = 7
  Radius = 16.9
  SecondAngle = 0
FEATURE [Part::Cylinder] Cylinder481
  Angle = 360
  AttacherType = Attacher::AttachEngine3D
  FirstAngle = 0
  Height = 1.2
  Radius = 50
  SecondAngle = 0
FEATURE [Part::Cylinder] Cylinder482
  Angle = 360
  AttacherType = Attacher::AttachEngine3D
  FirstAngle = 0
  Height = 70
  Placement = pos=(0,-22.5,41) rot=(0,0,1;1.25664rad)
  Radius = 39.4
  SecondAngle = 0
FEATURE [Part::Cylinder] Cylinder483
  Angle = 360
  AttacherType = Attacher::AttachEngine3D
  FirstAngle = 0
  Height = 70
  Placement = pos=(0,-22.5,41) rot=(0,0,1;1.25664rad)
  Radius = 38.6
  SecondAngle = 0
FEATURE [Part::Cut] Cut227
  Base = -> Cylinder482
  Tool = -> Cylinder483
FEATURE [Part::Cut] Cut228
  Base = -> Cut227
  Tool = -> Box081
FEATURE [Part::Cylinder] Cylinder484
  Angle = 360
  AttacherType = Attacher::AttachEngine3D
  FirstAngle = 0
  Height = 70
  Placement = pos=(0,0,41) rot=(0,0,1;0rad)
  Radius = 50
  SecondAngle = 0
FEATURE [Part::MultiCommon] Common032
  Shapes = -> [Cut228,Cylinder484]
FEATURE [Part::Cylinder] Cylinder485
  Angle = 360
  AttacherType = Attacher::AttachEngine3D
  FirstAngle = 0
  Height = 70
  Placement = pos=(0,-22.5,41) rot=(0,0,1;1.25664rad)
  Radius = 39.4
  SecondAngle = 0
FEATURE [Part::Cylinder] Cylinder486
  Angle = 360
  AttacherType = Attacher::AttachEngine3D
  FirstAngle = 0
  Height = 70
  Placement = pos=(0,-22.5,41) rot=(0,0,1;1.25664rad)
  Radius = 38.6
  SecondAngle = 0
FEATURE [Part::Cut] Cut229
  Base = -> Cylinder485
  Tool = -> Cylinder486
FEATURE [Part::Cut] Cut230
  Base = -> Cut229
  Tool = -> Box082
FEATURE [Part::Cylinder] Cylinder487
  Angle = 360
  AttacherType = Attacher::AttachEngine3D
  FirstAngle = 0
  Height = 70
  Placement = pos=(0,0,41) rot=(0,0,1;0rad)
  Radius = 50
  SecondAngle = 0
FEATURE [Part::MultiCommon] Common033
  Placement = pos=(0,0,0) rot=(0,0,1;1.25664rad)
  Shapes = -> [Cut230,Cylinder487]
FEATURE [Part::Cylinder] Cylinder488
  Angle = 360
  AttacherType = Attacher::AttachEngine3D
  FirstAngle = 0
  Height = 70
  Placement = pos=(0,-22.5,41) rot=(0,0,1;1.25664rad)
  Radius = 39.4
  SecondAngle = 0
FEATURE [Part::Cylinder] Cylinder489
  Angle = 360
  AttacherType = Attacher::AttachEngine3D
  FirstAngle = 0
  Height = 70
  Placement = pos=(0,-22.5,41) rot=(0,0,1;1.25664rad)
  Radius = 38.6
  SecondAngle = 0
FEATURE [Part::Cut] Cut231
  Base = -> Cylinder488
  Tool = -> Cylinder489
FEATURE [Part::Cut] Cut232
  Base = -> Cut231
  Tool = -> Box083
FEATURE [Part::Cylinder] Cylinder490
  Angle = 360
  AttacherType = Attacher::AttachEngine3D
  FirstAngle = 0
  Height = 70
  Placement = pos=(0,0,41) rot=(0,0,1;0rad)
  Radius = 50
  SecondAngle = 0
FEATURE [Part::MultiCommon] Common034
  Placement = pos=(0,0,0) rot=(0,0,1;2.51327rad)
  Shapes = -> [Cut232,Cylinder490]
FEATURE [Part::Cylinder] Cylinder491
  Angle = 360
  AttacherType = Attacher::AttachEngine3D
  FirstAngle = 0
  Height = 70
  Placement = pos=(0,-22.5,41) rot=(0,0,1;1.25664rad)
  Radius = 39.4
  SecondAngle = 0
FEATURE [Part::Cylinder] Cylinder492
  Angle = 360
  AttacherType = Attacher::AttachEngine3D
  FirstAngle = 0
  Height = 70
  Placement = pos=(0,-22.5,41) rot=(0,0,1;1.25664rad)
  Radius = 38.6
  SecondAngle = 0
FEATURE [Part::Cut] Cut233
  Base = -> Cylinder491
  Tool = -> Cylinder492
FEATURE [Part::Cut] Cut234
  Base = -> Cut233
  Tool = -> Box084
FEATURE [Part::Cylinder] Cylinder493
  Angle = 360
  AttacherType = Attacher::AttachEngine3D
  FirstAngle = 0
  Height = 70
  Placement = pos=(0,0,41) rot=(0,0,1;0rad)
  Radius = 50
  SecondAngle = 0
FEATURE [Part::MultiCommon] Common035
  Placement = pos=(0,0,0) rot=(0,0,1;3.76991rad)
  Shapes = -> [Cut234,Cylinder493]
FEATURE [Part::Cylinder] Cylinder494
  Angle = 360
  AttacherType = Attacher::AttachEngine3D
  FirstAngle = 0
  Height = 70
  Placement = pos=(0,-22.5,41) rot=(0,0,1;1.25664rad)
  Radius = 39.4
  SecondAngle = 0
FEATURE [Part::Cylinder] Cylinder495
  Angle = 360
  AttacherType = Attacher::AttachEngine3D
  FirstAngle = 0
  Height = 70
  Placement = pos=(0,-22.5,41) rot=(0,0,1;1.25664rad)
  Radius = 38.6
  SecondAngle = 0
FEATURE [Part::Cut] Cut235
  Base = -> Cylinder494
  Tool = -> Cylinder495
FEATURE [Part::Cut] Cut236
  Base = -> Cut235
  Tool = -> Box085
FEATURE [Part::Cylinder] Cylinder496
  Angle = 360
  AttacherType = Attacher::AttachEngine3D
  FirstAngle = 0
  Height = 70
  Placement = pos=(0,0,41) rot=(0,0,1;0rad)
  Radius = 50
  SecondAngle = 0
FEATURE [Part::MultiCommon] Common036
  Placement = pos=(0,0,0) rot=(0,0,-1;1.25664rad)
  Shapes = -> [Cut236,Cylinder496]
FEATURE [Part::Cylinder] Cylinder497
  Angle = 360
  AttacherType = Attacher::AttachEngine3D
  FirstAngle = 0
  Height = 7
  Radius = 16.1
  SecondAngle = 0
FEATURE [Part::Cylinder] Cylinder498
  Angle = 360
  AttacherType = Attacher::AttachEngine3D
  FirstAngle = 0
  Height = 7
  Radius = 16.9
  SecondAngle = 0
FEATURE [Part::Cylinder] Cylinder499
  Angle = 360
  AttacherType = Attacher::AttachEngine3D
  FirstAngle = 0
  Height = 1.2
  Radius = 50
  SecondAngle = 0
FEATURE [Part::MultiFuse] Fusion252
  Shapes = -> [Cylinder480,Cylinder481]
FEATURE [Part::Cut] Cut237
  Base = -> Fusion252
  Placement = pos=(0,0,40) rot=(0,0,1;0rad)
  Tool = -> Cylinder479
FEATURE [Part::MultiFuse] Fusion253
  Shapes = -> [Common032,Common033,Common034,Common035,Common036]
FEATURE [Part::MultiFuse] Fusion254  label="blattom"
  Shapes = -> [Cut237,Fusion253]
FEATURE [Part::MultiFuse] Fusion255
  Shapes = -> [Cylinder498,Cylinder499]
FEATURE [Part::Cut] Cut238  label="blades-top"
  Base = -> Fusion255
  Placement = pos=(0,0,112.2) rot=(1,0,0;3.14159rad)
  Tool = -> Cylinder497
FEATURE [Part::Cylinder] Cylinder645
  Angle = 360
  AttacherType = Attacher::AttachEngine3D
  FirstAngle = 0
  Height = 1.5
  Radius = 20
  SecondAngle = 0
FEATURE [Part::Cylinder] Cylinder646
  Angle = 360
  AttacherType = Attacher::AttachEngine3D
  FirstAngle = 0
  Height = 3
  Radius = 17
  SecondAngle = 0
FEATURE [Part::Cut] Cut286  label="guiding aid001"
  Base = -> Cylinder645
  Placement = pos=(125,3,175) rot=(1,0,0;1.5708rad)
  Tool = -> Cylinder646
FEATURE [Part::Cylinder] Cylinder647
  Angle = 360
  AttacherType = Attacher::AttachEngine3D
  FirstAngle = 0
  Height = 1.5
  Radius = 20
  SecondAngle = 0
FEATURE [Part::Cylinder] Cylinder648
  Angle = 360
  AttacherType = Attacher::AttachEngine3D
  FirstAngle = 0
  Height = 3
  Radius = 17
  SecondAngle = 0
FEATURE [Part::Cut] Cut287  label="guiding aid002"
  Base = -> Cylinder647
  Placement = pos=(125,-0.5,175) rot=(1,0,0;1.5708rad)
  Tool = -> Cylinder648
FEATURE [Part::MultiFuse] Fusion315
  Shapes = -> [Cut219,Cut286,Cut287]
FEATURE [Part::Fillet] Fillet103  label="guiding aid"
  Base = -> Fusion315
  EdgeLinks = -> Fusion315 [Edge8,Edge9,Edge11,Edge13,Edge14,Edge15]
  Edges = 6 edges r=0.74: [Edge8,Edge9,Edge11,Edge13,Edge14,Edge15]
FEATURE [Part::Part2DObjectPython] VThreadProfile006  # Draft 2D object (typed FeaturePython)
  Area = 178.439
  Closed = true
  Continuity = C2
  Height = 10
  Helix = Helix
  Instructions = <same value as first occurrence — deduplicated (x6 in doc)>
  InternalOrExternal = 1
  MakeFace = true
  MinorDiameter = 14.15
  Parameterization = 1
  Pitch = 2
  Points = (66) [(7.03765,0.678597,0),(6.89909,1.34296,0),(6.70966,1.99042,0),(6.46679,2.61677,0),(6.17068,3.21749,0),(5.82283,3.78803,0),(5.42556,4.32397,0),+59 more]
  Presets = 0
  Quality = 11
  ThreadCount = 5
  Variants = 0
  Version = 1.89
  external2S_data = <same value as first occurrence — deduplicated (x6 in doc)>
  external3S_data = <same value as first occurrence — deduplicated (x6 in doc)>
  external45_data = <same value as first occurrence — deduplicated (x6 in doc)>
  external_data = <same value as first occurrence — deduplicated (x6 in doc)>
  internal2S_data = <same value as first occurrence — deduplicated (x6 in doc)>
  internal3S_data = <same value as first occurrence — deduplicated (x6 in doc)>
  internal45_data = <same value as first occurrence — deduplicated (x6 in doc)>
  internal_data = <same value as first occurrence — deduplicated (x6 in doc)>
  preset_names = <blob: 3959 chars omitted>
  presets_data = <same value as first occurrence — deduplicated (x6 in doc)>
FEATURE [Part::Cone] Cone023
  Angle = 360
  AttacherType = Attacher::AttachEngine3D
  Height = 14
  Placement = pos=(0,0,26) rot=(0,0,1;0rad)
  Radius1 = 8
  Radius2 = 11.5
FEATURE [Part::Cone] Cone024 .. Cone028  x5 (patterned run collapsed; names and placements below)
  Angle = 360
  AttacherType = Attacher::AttachEngine3D
  Height = 14
  Radius1 = 5
  Radius2 = 2
  placements: all 5 at pos=(12.5,0,26) rot=(0,0,1;0rad)
FEATURE [Part::Cut] Cut288
  Base = -> Cone023
  Placement = pos=(0,0,0) rot=(0,0,1;1.25664rad)
  Tool = -> Cone024
FEATURE [Part::Cut] Cut289
  Base = -> Cut288
  Placement = pos=(0,0,0) rot=(0,0,1;1.25664rad)
  Tool = -> Cone025
FEATURE [Part::Cut] Cut290
  Base = -> Cut289
  Placement = pos=(0,0,0) rot=(0,0,1;1.25664rad)
  Tool = -> Cone027
FEATURE [Part::Cut] Cut291
  Base = -> Cut290
  Placement = pos=(0,0,0) rot=(0,0,1;1.25664rad)
  Tool = -> Cone026
FEATURE [Part::Cut] Cut292
  Base = -> Cut291
  Tool = -> Cone028
FEATURE [Part::Cylinder] Cylinder652
  Angle = 360
  AttacherType = Attacher::AttachEngine3D
  FirstAngle = 0
  Height = 21
  Placement = pos=(0,0,26) rot=(0,0,1;0rad)
  Radius = 4.5
  SecondAngle = 0
FEATURE [Part::Helix] Helix022
  Angle = 0
  AttacherType = Attacher::AttachEngine3D
  Height = 10
  Length = 231.123
  LocalCoord = 0
  Pitch = 2
  Radius = 7.35
  SegmentLength = 1
  Style = 0
  expr: AttachmentOffset = VThreadProfile041.AttachmentOffset
  expr: Height = VThreadProfile042.ThreadCount * VThreadProfile042.Pitch
  expr: MapMode = VThreadProfile041.MapMode
  expr: MapPathParameter = VThreadProfile041.MapPathParameter
  expr: MapReversed = VThreadProfile041.MapReversed
  expr: Pitch = VThreadProfile042.Pitch
  expr: SegmentLength = 1
FEATURE [Part::Part2DObjectPython] VThreadProfile041  # Draft 2D object (typed FeaturePython)
  Area = 163.406
  Closed = true
  Continuity = C2
  Height = 10
  Helix = Helix
  Instructions = <same value as first occurrence — deduplicated (x6 in doc)>
  InternalOrExternal = 1
  MakeFace = true
  MinorDiameter = 13.5
  Parameterization = 1
  Pitch = 2
  Points = (66) [(6.71415,0.647404,0),(6.58007,1.28086,0),(6.39808,1.89799,0),(6.16552,2.49486,0),(5.8825,3.06723,0),(5.55041,3.6108,0),(5.1714,4.12141,0),+59 more]
  Presets = 0
  Quality = 11
  ThreadCount = 5
  Variants = 0
  Version = 1.89
  external2S_data = <same value as first occurrence — deduplicated (x6 in doc)>
  external3S_data = <same value as first occurrence — deduplicated (x6 in doc)>
  external45_data = <same value as first occurrence — deduplicated (x6 in doc)>
  external_data = <same value as first occurrence — deduplicated (x6 in doc)>
  internal2S_data = <same value as first occurrence — deduplicated (x6 in doc)>
  internal3S_data = <same value as first occurrence — deduplicated (x6 in doc)>
  internal45_data = <same value as first occurrence — deduplicated (x6 in doc)>
  internal_data = <same value as first occurrence — deduplicated (x6 in doc)>
  preset_names = <blob: 3959 chars omitted>
  presets_data = <same value as first occurrence — deduplicated (x6 in doc)>
FEATURE [Part::Sweep] Sweep022  label="m16 thread016"
  Frenet = true
  Placement = pos=(0,0,37) rot=(0,0,1;0rad)
  Sections = -> [VThreadProfile041]
  Solid = true
  Spine = -> Helix022 [Edge1,Edge2,Edge3,Edge4,Edge5]
  Transition = 1
FEATURE [Part::MultiFuse] Fusion320
  Shapes = -> [Sweep022,Cut292]
FEATURE [Part::Cut] Cut293
  Base = -> Fusion320
  Tool = -> Cylinder652
FEATURE [Part::Fillet] Fillet104  label="bottom-screw-prefinal001"
  Base = -> Cut293
  EdgeLinks = -> Cut293 [Edge4,Edge5,Edge6,Edge7,Edge8,Edge9,Edge10,Edge11,Edge12,Edge13]
  Edges = 10 edges r=0.5: [Edge4,Edge5,Edge6,Edge7,Edge8,Edge9,Edge10,Edge11,Edge12,Edge13]
FEATURE [Part::Fillet] Fillet105  label="bottom-screw001"
  Base = -> Fillet104
  EdgeLinks = -> Fillet104 [Edge44,Edge46,Edge47,Edge50,Edge52,Edge53,Edge55,Edge58,Edge60,Edge61]
  Edges = 10 edges r=1: [Edge44,Edge46,Edge47,Edge50,Edge52,Edge53,Edge55,Edge58,Edge60,Edge61]
FEATURE [Part::Part2DObjectPython] VThreadProfile042  # Draft 2D object (typed FeaturePython)
  Area = 178.439
  Closed = true
  Continuity = C2
  Height = 10
  Helix = Helix
  Instructions = <same value as first occurrence — deduplicated (x6 in doc)>
  InternalOrExternal = 1
  MakeFace = true
  MinorDiameter = 14.15
  Parameterization = 1
  Pitch = 2
  Points = (66) [(7.03765,0.678597,0),(6.89909,1.34296,0),(6.70966,1.99042,0),(6.46679,2.61677,0),(6.17068,3.21749,0),(5.82283,3.78803,0),(5.42556,4.32397,0),+59 more]
  Presets = 0
  Quality = 11
  ThreadCount = 5
  Variants = 0
  Version = 1.89
  external2S_data = <same value as first occurrence — deduplicated (x6 in doc)>
  external3S_data = <same value as first occurrence — deduplicated (x6 in doc)>
  external45_data = <same value as first occurrence — deduplicated (x6 in doc)>
  external_data = <same value as first occurrence — deduplicated (x6 in doc)>
  internal2S_data = <same value as first occurrence — deduplicated (x6 in doc)>
  internal3S_data = <same value as first occurrence — deduplicated (x6 in doc)>
  internal45_data = <same value as first occurrence — deduplicated (x6 in doc)>
  internal_data = <same value as first occurrence — deduplicated (x6 in doc)>
  preset_names = <blob: 3959 chars omitted>
  presets_data = <same value as first occurrence — deduplicated (x6 in doc)>
FEATURE [Part::Cylinder] Cylinder653
  Angle = 360
  AttacherType = Attacher::AttachEngine3D
  FirstAngle = 0
  Height = 70
  Placement = pos=(49.2,5.5,41) rot=(0,0,1;0rad)
  Radius = 0.5
  SecondAngle = 0
FEATURE [Part::Box] Box125  label="Cube124"
  AttacherType = Attacher::AttachEngine3D
  Height = 70
  Length = 0.89
  Placement = pos=(48.91,3.48,41) rot=(0,0,1;0.10472rad)
  Width = 2
FEATURE [Part::MultiFuse] Fusion321
  Shapes = -> [Box125,Cylinder653]
FEATURE [Part::Box] Box126  label="Cube125"
  AttacherType = Attacher::AttachEngine3D
  Height = 70
  Length = 0.89
  Placement = pos=(48.91,3.48,41) rot=(0,0,1;0.10472rad)
  Width = 2
FEATURE [Part::Cylinder] Cylinder654
  Angle = 360
  AttacherType = Attacher::AttachEngine3D
  FirstAngle = 0
  Height = 70
  Placement = pos=(49.2,5.5,41) rot=(0,0,1;0rad)
  Radius = 0.5
  SecondAngle = 0
FEATURE [Part::MultiFuse] Fusion322
  Placement = pos=(0,0,0) rot=(0,0,1;1.25664rad)
  Shapes = -> [Box126,Cylinder654]
FEATURE [Part::Box] Box127  label="Cube126"
  AttacherType = Attacher::AttachEngine3D
  Height = 70
  Length = 0.89
  Placement = pos=(48.91,3.48,41) rot=(0,0,1;0.10472rad)
  Width = 2
FEATURE [Part::Cylinder] Cylinder655
  Angle = 360
  AttacherType = Attacher::AttachEngine3D
  FirstAngle = 0
  Height = 70
  Placement = pos=(49.2,5.5,41) rot=(0,0,1;0rad)
  Radius = 0.5
  SecondAngle = 0
FEATURE [Part::MultiFuse] Fusion323
  Placement = pos=(0,0,0) rot=(0,0,1;2.51327rad)
  Shapes = -> [Box127,Cylinder655]
FEATURE [Part::Box] Box128  label="Cube127"
  AttacherType = Attacher::AttachEngine3D
  Height = 70
  Length = 0.89
  Placement = pos=(48.91,3.48,41) rot=(0,0,1;0.10472rad)
  Width = 2
FEATURE [Part::Cylinder] Cylinder656
  Angle = 360
  AttacherType = Attacher::AttachEngine3D
  FirstAngle = 0
  Height = 70
  Placement = pos=(49.2,5.5,41) rot=(0,0,1;0rad)
  Radius = 0.5
  SecondAngle = 0
FEATURE [Part::MultiFuse] Fusion324
  Placement = pos=(0,0,0) rot=(0,0,1;3.76991rad)
  Shapes = -> [Box128,Cylinder656]
FEATURE [Part::Box] Box129  label="Cube128"
  AttacherType = Attacher::AttachEngine3D
  Height = 70
  Length = 0.89
  Placement = pos=(48.91,3.48,41) rot=(0,0,1;0.10472rad)
  Width = 2
FEATURE [Part::Cylinder] Cylinder657
  Angle = 360
  AttacherType = Attacher::AttachEngine3D
  FirstAngle = 0
  Height = 70
  Placement = pos=(49.2,5.5,41) rot=(0,0,1;0rad)
  Radius = 0.5
  SecondAngle = 0
FEATURE [Part::MultiFuse] Fusion325
  Placement = pos=(0,0,0) rot=(0,0,1;5.02655rad)
  Shapes = -> [Box129,Cylinder657]
FEATURE [Part::MultiFuse] Fusion326
  Shapes = -> [Fusion321,Fusion322,Fusion323,Fusion324,Fusion325]
FEATURE [Part::MultiFuse] Fusion327  label="blades-bottom"
  Shapes = -> [Fusion254,Fusion326]
